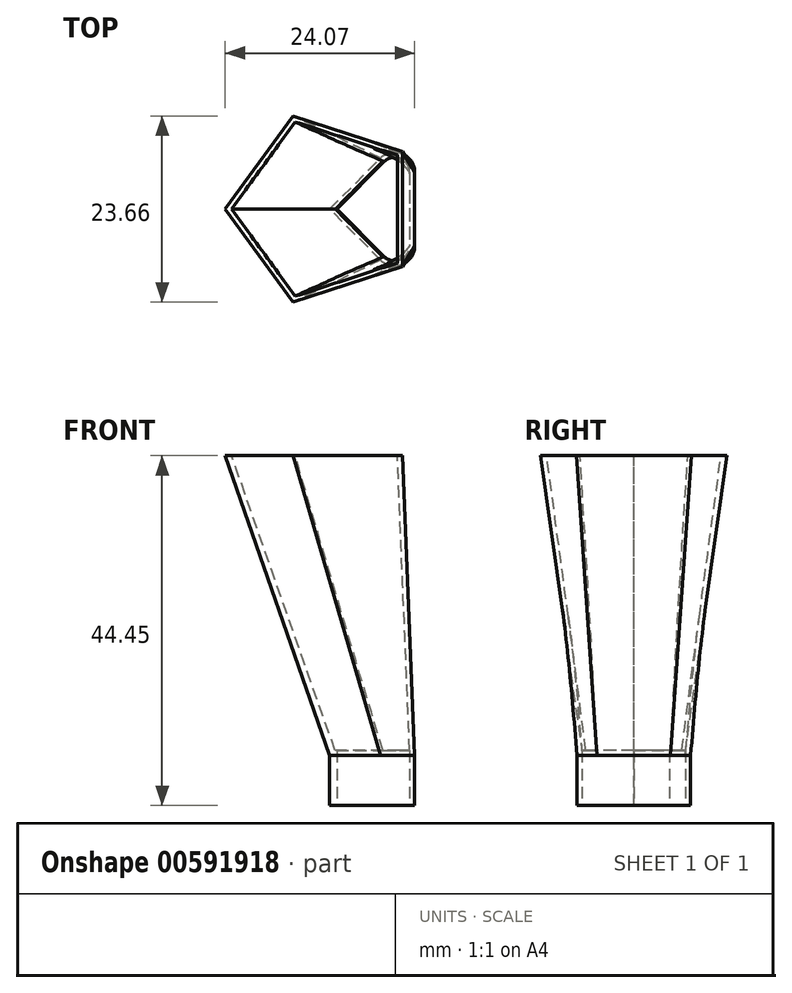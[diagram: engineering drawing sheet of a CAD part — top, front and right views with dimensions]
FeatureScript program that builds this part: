
annotation { "Feature Type Name" : "Feature", "Feature Type Description" : "" }
export const myFeature = defineFeature(function(context is Context, id is Id, definition is map)
    precondition{}
    {
        {
            var Q0;
            Q0=qCreatedBy(makeId("Top.planeOp"),FACE);
            var sketch = newSketch(context, id + "F0", { "sketchPlane" : qUnion([Q0])});
            skLineSegment(sketch, "E0", {"start": v(56.2, -6.47) * mm, "end": v(49.74, 0) * mm});
            skLineSegment(sketch, "E1", {"start": v(49.74, 0) * mm, "end": v(56.2, 6.47) * mm});
            skLineSegment(sketch, "E2", {"start": v(60.54, 4.67) * mm, "end": v(60.54, -4.67) * mm});
            skArc(sketch, "E3", {"start": v(60.54, 4.67) * mm, "mid": v(58.97, 7.02) * mm, "end": v(56.2, 6.47) * mm});
            skArc(sketch, "E4", {"start": v(56.2, -6.47) * mm, "mid": v(58.97, -7.02) * mm, "end": v(60.54, -4.67) * mm});
            skSolve(sketch);
        }
        {
            var Q0;
            Q0=qCreatedBy(makeId("Top.planeOp"),FACE);
            cPlane(context, id + "F1", {"entities" : qUnion([Q0]), "cplaneType" : CPlaneType.OFFSET, "offset" : 38.1 * mm, "width" : 152.4 * mm, "height" : 152.4 * mm});
        }
        {
            var Q0;
            Q0=qCreatedBy(id+"F1.planeOp",FACE);
            var sketch = newSketch(context, id + "F2", { "sketchPlane" : qUnion([Q0])});
            skCircle(sketch, "E5.cCircle", {"center": v(48.92, 0) * mm, "radius": 10.07 * mm, "construction": true});
            skLineSegment(sketch, "E5.0", {"start": v(58.98, 7.31) * mm, "end": v(58.98, -7.31) * mm});
            skLineSegment(sketch, "E5.1", {"start": v(58.98, -7.31) * mm, "end": v(45.07, -11.83) * mm});
            skLineSegment(sketch, "E5.2", {"start": v(45.07, -11.83) * mm, "end": v(36.47, 0) * mm});
            skLineSegment(sketch, "E5.3", {"start": v(36.47, 0) * mm, "end": v(45.07, 11.83) * mm});
            skLineSegment(sketch, "E5.4", {"start": v(45.07, 11.83) * mm, "end": v(58.98, 7.31) * mm});
            skPoint(sketch, "E5.0.midPoint", {"position": v(58.98, 0) * mm});
            skSolve(sketch);
        }
        {
            var Q0;
            Q0=qSketchRegion(id+"F0",true);
            var Q1;
            Q1=qSketchRegion(id+"F2",true);
            loft(context, id + "F3", {"sheetProfilesArray" : [{ "sheetProfileEntities" : qUnion([Q0]) }, { "sheetProfileEntities" : qUnion([Q1]) }]});
        }
        {
            var Q0;
            Q0=makeQuery(id+"F3.opLoft","CAP_FACE",FACE,{"disambiguationData":[OSD([makeQuery(id+"F2.imprint","IMPRINT",FACE,{"disambiguationData":[TD([[makeQuery(id+"F2.imprint","IMPRINT",EDGE,{"derivedFrom":sQuery(id+"F2.wireOp",EDGE,"E5.0")}),-1.0]])]})])],"isStart":true});
            shell(context, id + "F4", {"entities" : qUnion([Q0]), "thickness" : 0.64 * mm});
        }
        {
            var Q0;
            Q0=makeQuery(id+"F3.opLoft","CAP_FACE",FACE,{"disambiguationData":[OSD([makeQuery(id+"F0.imprint","IMPRINT",FACE,{"disambiguationData":[TD([[makeQuery(id+"F0.imprint","IMPRINT",EDGE,{"derivedFrom":sQuery(id+"F0.wireOp",EDGE,"E0")}),-1.0]])]})])],"isStart":true});
            var sketch = newSketch(context, id + "F5", { "sketchPlane" : qUnion([Q0])});
            skLineSegment(sketch, "E6", {"start": v(50.64, 0) * mm, "end": v(56.65, -6.02) * mm});
            skLineSegment(sketch, "E7", {"start": v(50.64, 0) * mm, "end": v(56.65, 6.02) * mm});
            skArc(sketch, "E8", {"start": v(59.9, 4.67) * mm, "mid": v(58.73, 6.43) * mm, "end": v(56.65, 6.02) * mm});
            skArc(sketch, "E9", {"start": v(56.65, -6.02) * mm, "mid": v(58.8, -6.4) * mm, "end": v(59.9, -4.52) * mm});
            skLineSegment(sketch, "E10", {"start": v(59.9, -4.52) * mm, "end": v(59.9, 4.67) * mm});
            skSolve(sketch);
        }
        {
            var Q0;
            Q0=qSketchRegion(id+"F5",true);
            extrude(context, id + "F6", {"entities" : qUnion([Q0]), "operationType" : NewBodyOperationType.REMOVE, "oppositeDirection" : true, "depth" : 0.64 * mm, "offsetDistance" : 25.4 * mm});
        }
        {
            var Q0;
            Q0=qSketchRegion(id+"F0",true);
            extrude(context, id + "F7", {"entities" : qUnion([Q0]), "operationType" : NewBodyOperationType.ADD, "oppositeDirection" : true, "depth" : 6.35 * mm, "offsetDistance" : 25.4 * mm});
        }
        {
            var Q0;
            Q0=qSketchRegion(id+"F5",true);
            extrude(context, id + "F8", {"entities" : qUnion([Q0]), "operationType" : NewBodyOperationType.REMOVE, "endBound" : BoundingType.UP_TO_NEXT, "depth" : 25.4 * mm, "offsetDistance" : 25.4 * mm});
        }
    });
